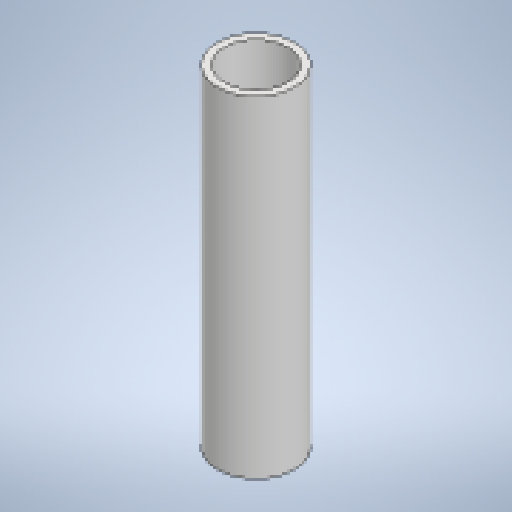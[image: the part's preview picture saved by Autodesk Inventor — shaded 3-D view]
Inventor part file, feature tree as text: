
AUTODESK INVENTOR PART (.ipt)
format: ipt  version: 2025.1 (Build 291241020, 241B)  size: 171,008 bytes
history: native  units: mm
features: extrude x1, sketch x1
ambient origin geometry x8: Origin, YZ Plane, XZ Plane, XY Plane, X Axis, Y Axis, Z Axis, Center Point
bodies: Body1 (feature_tree)
feature tree (2):
  extrude  "Extrusion5"  Depth=90.0mm
  sketch  "Sketch11"  dims[d187=21.0mm d188=2.0mm d189=90.0mm d190=0.0mm]
